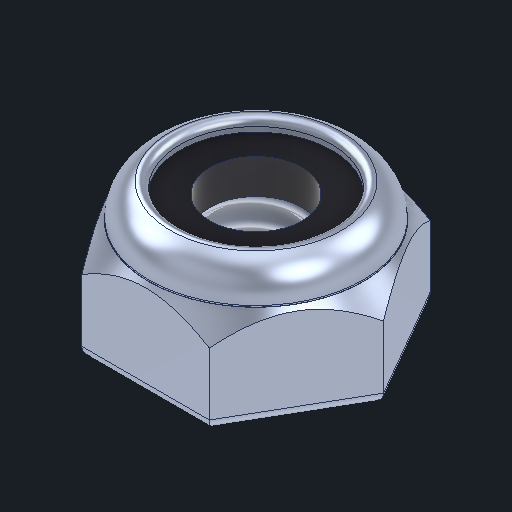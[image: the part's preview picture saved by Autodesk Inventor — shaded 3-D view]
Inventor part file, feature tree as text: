
AUTODESK INVENTOR PART (.ipt)
format: ipt  version: 2025 (Build 290162000, 162)  size: 226,816 bytes
history: native  units: in
note: dims shown in document units (in); Inventor stores cm internally (conversion verified against a paired STEP export)
features: other x4, sketch x2, plane x1
ambient origin geometry x8: Origin, YZ Plane, XZ Plane, XY Plane, X Axis, Y Axis, Z Axis, Center Point
bodies: Body1 (feature_tree)
feature tree (7):
  other  "Nut Thin Nylock.ipt"
  other  "NONE::Nut Thin Nylock.ipt"
  other  "TaggingFeature1"
  sketch  "Sketch1"  dims[d0=0.3937in]
  sketch  "Sketch2"
  plane  "Work Plane1"
  parser-record x1  (decoder bookkeeping rows leaked as tree rows — omitted from the tree; the rows remain in map.json)
